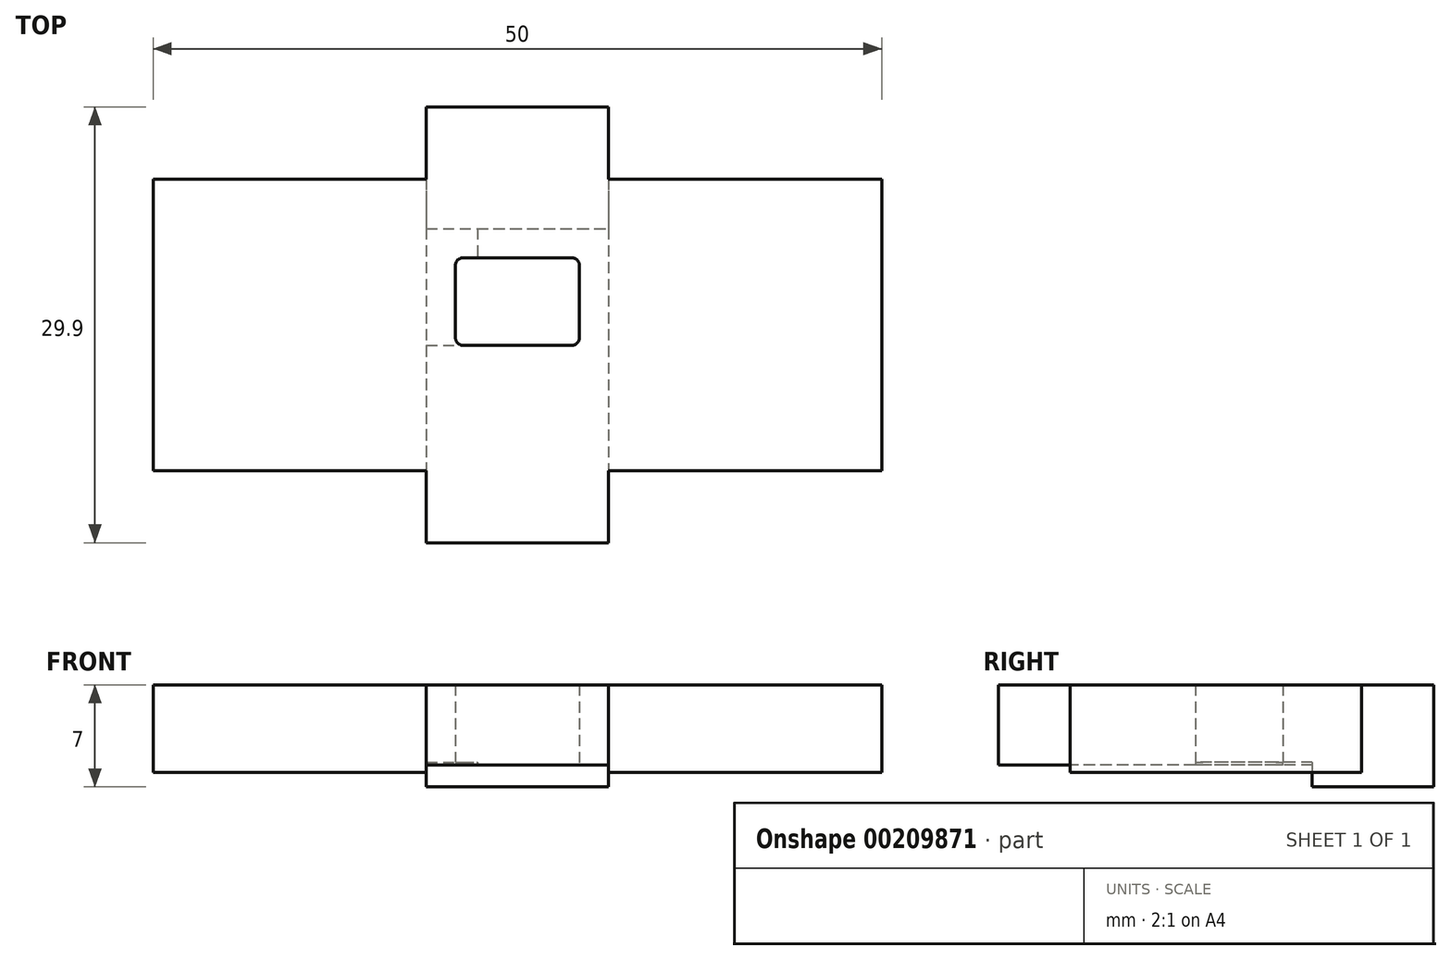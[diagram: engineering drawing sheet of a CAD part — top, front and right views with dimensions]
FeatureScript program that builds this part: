
annotation { "Feature Type Name" : "Feature", "Feature Type Description" : "" }
export const myFeature = defineFeature(function(context is Context, id is Id, definition is map)
    precondition{}
    {
        {
            var Q0;
            Q0=qCreatedBy(makeId("Top.planeOp"),FACE);
            var sketch = newSketch(context, id + "F0", { "sketchPlane" : qUnion([Q0])});
            skLineSegment(sketch, "E0.bottom", {"start": v(25, -10) * mm, "end": v(-25, -10) * mm});
            skLineSegment(sketch, "E0.top", {"start": v(25, 10) * mm, "end": v(-25, 10) * mm});
            skLineSegment(sketch, "E0.left", {"start": v(25, -10) * mm, "end": v(25, 10) * mm});
            skLineSegment(sketch, "E0.right", {"start": v(-25, -10) * mm, "end": v(-25, 10) * mm});
            skPoint(sketch, "E0.middle", {"position": v(0, 0) * mm});
            skSolve(sketch);
        }
        {
            var Q0;
            Q0 = qSketchRegion(id + "F0", true);
            extrude(context, id + "F1", {"entities" : qUnion([Q0]), "depth" : 6 * mm});
        }
        {
            var Q0;
            Q0=makeQuery(id+"F1.opExtrude","CAP_FACE",FACE,{"disambiguationData":[OSD([sQuery(id+"F0.wireOp",EDGE,"E0.bottom"),sQuery(id+"F0.wireOp",EDGE,"E0.top"),sQuery(id+"F0.wireOp",EDGE,"E0.left"),sQuery(id+"F0.wireOp",EDGE,"E0.right")])],"isStart":true});
            var sketch = newSketch(context, id + "F2", { "sketchPlane" : qUnion([Q0])});
            skLineSegment(sketch, "E1.bottom", {"start": v(-6.25, -14.95) * mm, "end": v(6.25, -14.95) * mm});
            skLineSegment(sketch, "E1.top", {"start": v(-6.25, 14.95) * mm, "end": v(6.25, 14.95) * mm});
            skLineSegment(sketch, "E1.left", {"start": v(-6.25, -14.95) * mm, "end": v(-6.25, 14.95) * mm});
            skLineSegment(sketch, "E1.right", {"start": v(6.25, -14.95) * mm, "end": v(6.25, 14.95) * mm});
            skPoint(sketch, "E1.middle", {"position": v(0, 0) * mm});
            skSolve(sketch);
        }
        {
            var Q0;
            Q0 = qSketchRegion(id + "F2", true);
            extrude(context, id + "F3", {"entities" : qUnion([Q0]), "operationType" : NewBodyOperationType.ADD, "oppositeDirection" : true, "depth" : 6 * mm});
        }
        {
            var Q0;
            Q0=makeQuery(id+"F3.boolean.opBoolean","MERGE",FACE,{"derivedFrom":[makeQuery(id+"F1.opExtrude","CAP_FACE",FACE,{"disambiguationData":[OSD([sQuery(id+"F0.wireOp",EDGE,"E0.bottom"),sQuery(id+"F0.wireOp",EDGE,"E0.top"),sQuery(id+"F0.wireOp",EDGE,"E0.left"),sQuery(id+"F0.wireOp",EDGE,"E0.right")])],"isStart":true}),makeQuery(id+"F3.opExtrude","CAP_FACE",FACE,{"disambiguationData":[OSD([sQuery(id+"F2.wireOp",EDGE,"E1.bottom"),sQuery(id+"F2.wireOp",EDGE,"E1.top"),sQuery(id+"F2.wireOp",EDGE,"E1.left"),sQuery(id+"F2.wireOp",EDGE,"E1.right")])],"isStart":true})]});
            var sketch = newSketch(context, id + "F4", { "sketchPlane" : qUnion([Q0])});
            skLineSegment(sketch, "E2.0", {"start": v(-6.25, -14.95) * mm, "end": v(6.25, -14.95) * mm});
            skLineSegment(sketch, "E3.0", {"start": v(6.25, -14.95) * mm, "end": v(6.25, -6.35) * mm});
            skLineSegment(sketch, "E4.0", {"start": v(-6.25, -14.95) * mm, "end": v(-6.25, -6.35) * mm});
            skLineSegment(sketch, "E5.0", {"start": v(-6.25, -6.35) * mm, "end": v(6.25, -6.35) * mm});
            skPoint(sketch, "E6.orphan", {"position": v(6.25, -10) * mm});
            skPoint(sketch, "E7.orphan", {"position": v(-6.25, -10) * mm});
            skSolve(sketch);
        }
        {
            var Q0;
            {var subQ18=sQuery(id+"F4.wireOp",EDGE,"E5.0");Q0=makeQuery(id+"F4.imprint","IMPRINT",FACE,{"disambiguationData":[TD([[makeQuery(id+"F4.imprint","IMPRINT",EDGE,{"derivedFrom":subQ18}),1.0]])]});}
            var sketch = newSketch(context, id + "F5", { "sketchPlane" : qUnion([Q0])});
            skLineSegment(sketch, "E8.0", {"start": v(-6.25, 14.95) * mm, "end": v(6.25, 14.95) * mm});
            skLineSegment(sketch, "E9.0", {"start": v(6.25, -6.6) * mm, "end": v(6.25, 14.95) * mm});
            skLineSegment(sketch, "E10.0", {"start": v(-6.25, -6.6) * mm, "end": v(-6.25, 14.95) * mm});
            skLineSegment(sketch, "E11.0", {"start": v(-6.25, -6.6) * mm, "end": v(6.25, -6.6) * mm});
            skPoint(sketch, "E12.orphan", {"position": v(6.25, 10) * mm});
            skPoint(sketch, "E13.orphan", {"position": v(-6.25, 10) * mm});
            skSolve(sketch);
        }
        {
            var Q0;
            Q0 = qSketchRegion(id + "F5", true);
            extrude(context, id + "F6", {"entities" : qUnion([Q0]), "operationType" : NewBodyOperationType.REMOVE, "oppositeDirection" : true, "depth" : .5 * mm});
        }
        {
            var Q0;
            Q0=makeQuery(id+"F3.boolean.opBoolean","MERGE",FACE,{"derivedFrom":[makeQuery(id+"F1.opExtrude","CAP_FACE",FACE,{"disambiguationData":[OSD([sQuery(id+"F0.wireOp",EDGE,"E0.bottom"),sQuery(id+"F0.wireOp",EDGE,"E0.top"),sQuery(id+"F0.wireOp",EDGE,"E0.left"),sQuery(id+"F0.wireOp",EDGE,"E0.right")])],"isStart":false}),makeQuery(id+"F3.opExtrude","CAP_FACE",FACE,{"disambiguationData":[OSD([sQuery(id+"F2.wireOp",EDGE,"E1.bottom"),sQuery(id+"F2.wireOp",EDGE,"E1.top"),sQuery(id+"F2.wireOp",EDGE,"E1.left"),sQuery(id+"F2.wireOp",EDGE,"E1.right")])],"isStart":false})]});
            var sketch = newSketch(context, id + "F7", { "sketchPlane" : qUnion([Q0])});
            skLineSegment(sketch, "E14.0", {"start": v(-6.25, -4.95) * mm, "end": v(6.25, -4.95) * mm, "construction": true});
            skCircle(sketch, "E15", {"center": v(0, -4.95) * mm, "radius": 1.43 * mm});
            skSolve(sketch);
        }
        {
            var Q0;
            Q0=makeQuery(id+"F6.boolean.opBoolean","COPY",FACE,{"derivedFrom":makeQuery(id+"F6.opExtrude","CAP_FACE",FACE,{"disambiguationData":[OSD([sQuery(id+"F5.wireOp",EDGE,"E8.0"),sQuery(id+"F5.wireOp",EDGE,"E9.0"),sQuery(id+"F5.wireOp",EDGE,"E10.0"),sQuery(id+"F5.wireOp",EDGE,"E11.0")])],"isStart":false})});
            var sketch = newSketch(context, id + "F8", { "sketchPlane" : qUnion([Q0])});
            skLineSegment(sketch, "E16.0", {"start": v(-6.25, -6.6) * mm, "end": v(6.25, -6.6) * mm});
            skLineSegment(sketch, "E17.0", {"start": v(-6.25, -6.6) * mm, "end": v(-6.25, 10) * mm});
            skLineSegment(sketch, "E18.0", {"start": v(-6.25, 1.4) * mm, "end": v(6.25, 1.4) * mm});
            skLineSegment(sketch, "E19.0", {"start": v(-2.75, -6.6) * mm, "end": v(-2.75, 10) * mm});
            skSolve(sketch);
        }
        {
            var Q0;
            Q0 = qSketchRegion(id + "F8", true);
            extrude(context, id + "F9", {"entities" : qUnion([Q0]), "operationType" : NewBodyOperationType.REMOVE, "oppositeDirection" : true, "depth" : .2 * mm});
        }
        {
            var Q0;
            Q0=makeQuery(id+"F3.boolean.opBoolean","MERGE",FACE,{"derivedFrom":[makeQuery(id+"F1.opExtrude","CAP_FACE",FACE,{"disambiguationData":[OSD([sQuery(id+"F0.wireOp",EDGE,"E0.bottom"),sQuery(id+"F0.wireOp",EDGE,"E0.top"),sQuery(id+"F0.wireOp",EDGE,"E0.left"),sQuery(id+"F0.wireOp",EDGE,"E0.right")])],"isStart":true}),makeQuery(id+"F3.opExtrude","CAP_FACE",FACE,{"disambiguationData":[OSD([sQuery(id+"F2.wireOp",EDGE,"E1.bottom"),sQuery(id+"F2.wireOp",EDGE,"E1.top"),sQuery(id+"F2.wireOp",EDGE,"E1.left"),sQuery(id+"F2.wireOp",EDGE,"E1.right")])],"isStart":true})]});
            var sketch = newSketch(context, id + "F10", { "sketchPlane" : qUnion([Q0])});
            skLineSegment(sketch, "E20.0", {"start": v(-6.25, -14.95) * mm, "end": v(6.25, -14.95) * mm});
            skLineSegment(sketch, "E21.0", {"start": v(6.25, -14.95) * mm, "end": v(6.25, -6.6) * mm});
            skLineSegment(sketch, "E22.0", {"start": v(-6.25, -14.95) * mm, "end": v(-6.25, -6.6) * mm});
            skLineSegment(sketch, "E23.0", {"start": v(-6.25, -6.6) * mm, "end": v(6.25, -6.6) * mm});
            skPoint(sketch, "E24.orphan", {"position": v(6.25, -10) * mm});
            skPoint(sketch, "E25.orphan", {"position": v(-6.25, -10) * mm});
            skLineSegment(sketch, "E26", {"start": v(-6.25, -10) * mm, "end": v(-6.25, -14.95) * mm});
            skSolve(sketch);
        }
        {
            var Q0;
            Q0 = qSketchRegion(id + "F10", true);
            extrude(context, id + "F11", {"entities" : qUnion([Q0]), "operationType" : NewBodyOperationType.ADD, "depth" : 1 * mm});
        }
        {
            var Q0;
            Q0=makeQuery(id+"F6.boolean.opBoolean","COPY",FACE,{"derivedFrom":makeQuery(id+"F6.opExtrude","CAP_FACE",FACE,{"disambiguationData":[OSD([sQuery(id+"F5.wireOp",EDGE,"E8.0"),sQuery(id+"F5.wireOp",EDGE,"E9.0"),sQuery(id+"F5.wireOp",EDGE,"E10.0"),sQuery(id+"F5.wireOp",EDGE,"E11.0")])],"isStart":false})});
            var sketch = newSketch(context, id + "F12", { "sketchPlane" : qUnion([Q0])});
            skLineSegment(sketch, "E27.0", {"start": v(-6.25, 1.4) * mm, "end": v(4.25, 1.4) * mm});
            skLineSegment(sketch, "E28.0", {"start": v(-4.25, -4.6) * mm, "end": v(6.25, -4.6) * mm});
            skLineSegment(sketch, "E29.0", {"start": v(4.25, -6.6) * mm, "end": v(4.25, 10) * mm});
            skLineSegment(sketch, "E30.0", {"start": v(-4.25, -6.6) * mm, "end": v(-4.25, 1.4) * mm});
            skPoint(sketch, "E31.orphan", {"position": v(-2.75, 1.4) * mm});
            skSolve(sketch);
        }
        {
            var Q0;
            Q0 = qSketchRegion(id + "F12", true);
            extrude(context, id + "F13", {"entities" : qUnion([Q0]), "operationType" : NewBodyOperationType.REMOVE, "oppositeDirection" : true, "depth" : 25 * mm});
        }
        {
            var Q0;
            Q0=makeQuery(id+"F13.boolean.opBoolean","COPY",EDGE,{"derivedFrom":makeQuery(id+"F13.opExtrude","SWEPT_EDGE",EDGE,{"disambiguationData":[OSD([sQuery(id+"F12.wireOp",EDGE,"E27.0"),sQuery(id+"F12.wireOp",EDGE,"E29.0")])]})});
            var Q1;
            Q1=makeQuery(id+"F13.boolean.opBoolean","COPY",EDGE,{"derivedFrom":makeQuery(id+"F13.opExtrude","SWEPT_EDGE",EDGE,{"disambiguationData":[OSD([sQuery(id+"F12.wireOp",EDGE,"E28.0"),sQuery(id+"F12.wireOp",EDGE,"E29.0")])]})});
            var Q2;
            Q2=makeQuery(id+"F13.boolean.opBoolean","COPY",EDGE,{"derivedFrom":makeQuery(id+"F13.opExtrude","SWEPT_EDGE",EDGE,{"disambiguationData":[OSD([sQuery(id+"F12.wireOp",EDGE,"E28.0"),sQuery(id+"F12.wireOp",EDGE,"E30.0")])]})});
            var Q3;
            Q3=makeQuery(id+"F13.boolean.opBoolean","COPY",EDGE,{"derivedFrom":makeQuery(id+"F13.opExtrude","SWEPT_EDGE",EDGE,{"disambiguationData":[OSD([sQuery(id+"F12.wireOp",EDGE,"E27.0"),sQuery(id+"F12.wireOp",EDGE,"E30.0")])]})});
            fillet(context, id + "F14", {"entities" : qUnion([Q0, Q1, Q2, Q3]), "radius" : .5 * mm, "tangentPropagation" : true, "allowEdgeOverflow" : false});
        }
    });
